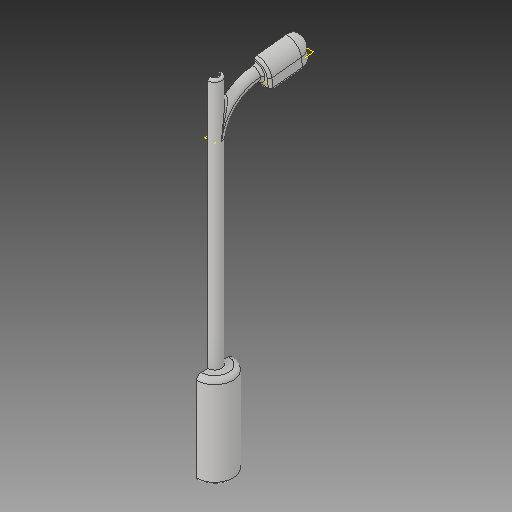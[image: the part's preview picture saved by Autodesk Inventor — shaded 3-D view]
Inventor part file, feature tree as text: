
AUTODESK INVENTOR PART (.ipt)
format: ipt  version: 2018 (Build 220112000, 112)  size: 369,664 bytes
history: native  units: in
note: dims shown in document units (in); Inventor stores cm internally (conversion verified against a paired STEP export)
features: sketch x10, other x3, plane x1
ambient origin geometry x8: Origin, YZ Plane, XZ Plane, XY Plane, X Axis, Y Axis, Z Axis, Center Point
bodies: Solid1 (feature_tree)
feature tree (14):
  other  "lampa.ipt"
  other  "Solid1::lampa.ipt"
  other  "TaggingFeature1"
  sketch  "Sketch1"  dims[d0=0.3937in]
  sketch  "Sketch6"
  sketch  "Sketch8"
  sketch  "Sketch9"
  sketch  "Sketch10"
  sketch  "Sketch11"
  sketch  "Sketch12"
  sketch  "Sketch13"
  sketch  "Sketch14"
  sketch  "Sketch15"
  plane  "Work Plane1"
